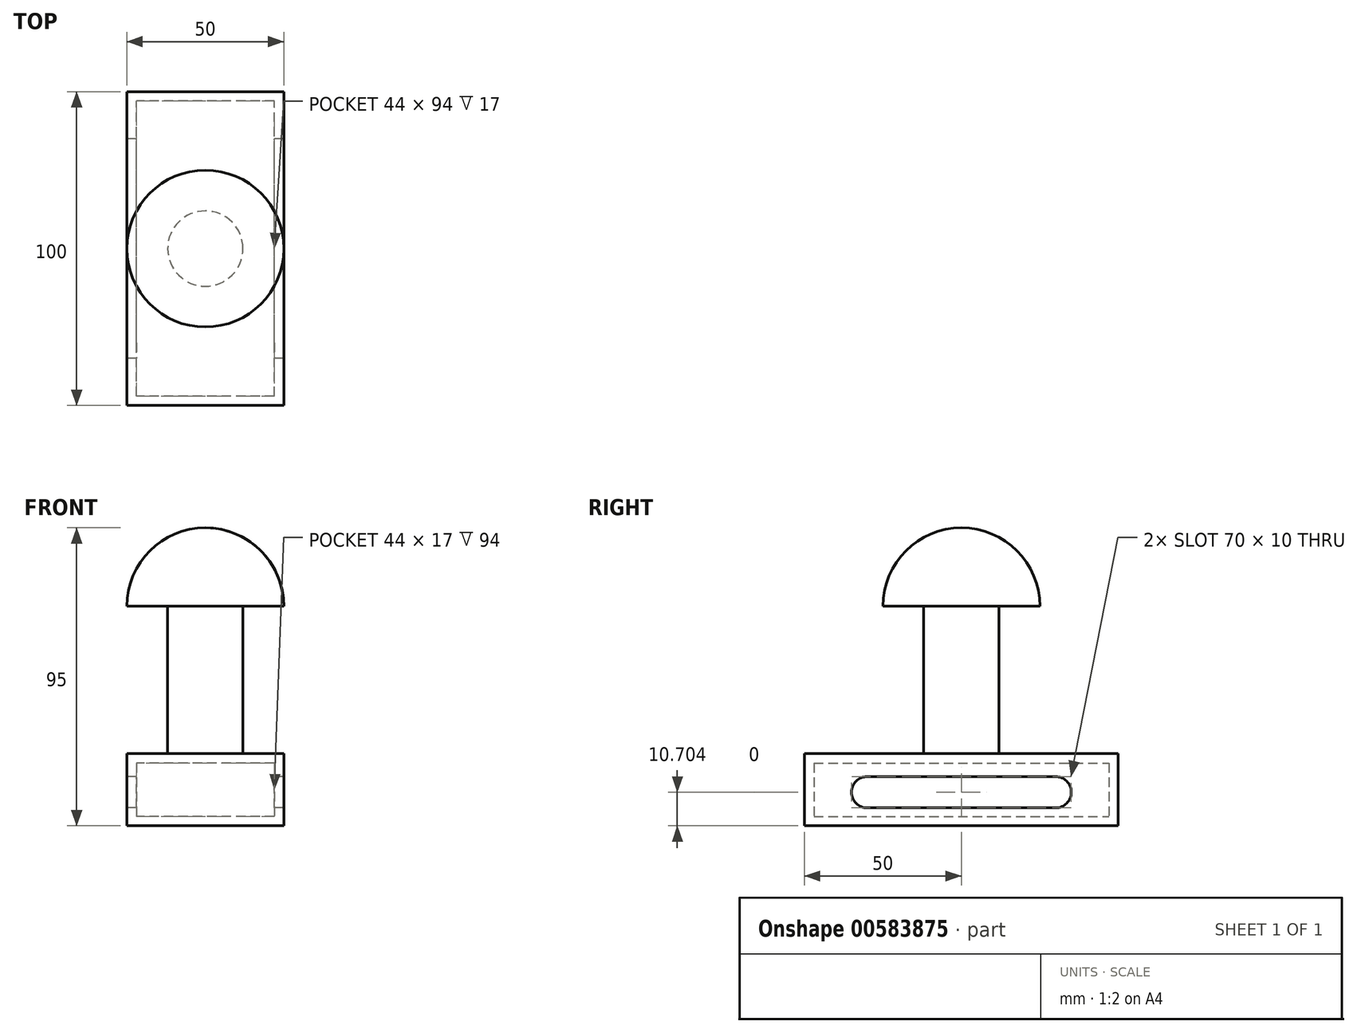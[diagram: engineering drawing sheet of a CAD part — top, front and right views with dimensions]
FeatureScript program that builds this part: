
annotation { "Feature Type Name" : "Feature", "Feature Type Description" : "" }
export const myFeature = defineFeature(function(context is Context, id is Id, definition is map)
    precondition{}
    {
        {
            var Q0;
            Q0=qCreatedBy(makeId("Top.planeOp"),FACE);
            var sketch = newSketch(context, id + "F0", { "sketchPlane" : qUnion([Q0])});
            skLineSegment(sketch, "E0.bottom", {"start": v(25, -50) * mm, "end": v(-25, -50) * mm});
            skLineSegment(sketch, "E0.top", {"start": v(25, 50) * mm, "end": v(-25, 50) * mm});
            skLineSegment(sketch, "E0.left", {"start": v(25, -50) * mm, "end": v(25, 50) * mm});
            skLineSegment(sketch, "E0.right", {"start": v(-25, -50) * mm, "end": v(-25, 50) * mm});
            skPoint(sketch, "E0.middle", {"position": v(0, 0) * mm});
            skLineSegment(sketch, "E1.bottom", {"start": v(22, -47) * mm, "end": v(-22, -47) * mm});
            skLineSegment(sketch, "E1.top", {"start": v(22, 47) * mm, "end": v(-22, 47) * mm});
            skLineSegment(sketch, "E1.left", {"start": v(22, -47) * mm, "end": v(22, 47) * mm});
            skLineSegment(sketch, "E1.right", {"start": v(-22, -47) * mm, "end": v(-22, 47) * mm});
            skSolve(sketch);
        }
        {
            var Q0;
            Q0 = qSketchRegion(id + "F0", true);
            extrude(context, id + "F1", {"entities" : qUnion([Q0]), "depth" : 20 * mm, "offsetDistance" : 25 * mm});
        }
        {
            var Q0;
            Q0=makeQuery(id+"F0.imprint","IMPRINT",FACE,{"disambiguationData":[TD([[makeQuery(id+"F0.imprint","IMPRINT",EDGE,{"derivedFrom":sQuery(id+"F0.wireOp",EDGE,"E1.bottom")}),-1.0]])]});
            var Q1;
            Q1=makeQuery(id+"F0.imprint","IMPRINT",FACE,{"disambiguationData":[TD([[makeQuery(id+"F0.imprint","IMPRINT",EDGE,{"derivedFrom":sQuery(id+"F0.wireOp",EDGE,"E0.bottom")}),-1.0]])]});
            extrude(context, id + "F2", {"entities" : qUnion([Q0, Q1]), "operationType" : NewBodyOperationType.ADD, "depth" : 3 * mm, "offsetDistance" : 25 * mm});
        }
        {
            var Q0;
            Q0=makeQuery(id+"F1.opExtrude","CAP_FACE",FACE,{"disambiguationData":[OSD([sQuery(id+"F0.wireOp",EDGE,"E0.bottom"),sQuery(id+"F0.wireOp",EDGE,"E0.top"),sQuery(id+"F0.wireOp",EDGE,"E0.left"),sQuery(id+"F0.wireOp",EDGE,"E0.right"),sQuery(id+"F0.wireOp",EDGE,"E1.bottom"),sQuery(id+"F0.wireOp",EDGE,"E1.top"),sQuery(id+"F0.wireOp",EDGE,"E1.left"),sQuery(id+"F0.wireOp",EDGE,"E1.right")])],"isStart":false});
            var sketch = newSketch(context, id + "F3", { "sketchPlane" : qUnion([Q0])});
            skLineSegment(sketch, "E2.bottom", {"start": v(-25, 50) * mm, "end": v(25, 50) * mm});
            skLineSegment(sketch, "E2.top", {"start": v(-25, -50) * mm, "end": v(25, -50) * mm});
            skLineSegment(sketch, "E2.left", {"start": v(-25, 50) * mm, "end": v(-25, -50) * mm});
            skLineSegment(sketch, "E2.right", {"start": v(25, 50) * mm, "end": v(25, -50) * mm});
            skCircle(sketch, "E3", {"center": v(0, 0) * mm, "radius": 25 * mm});
            skCircle(sketch, "E4", {"center": v(0, 0) * mm, "radius": 12 * mm});
            skSolve(sketch);
        }
        {
            var Q0;
            Q0=makeQuery(id+"F3.imprint","IMPRINT",FACE,{"disambiguationData":[TD([[makeQuery(id+"F3.imprint","IMPRINT",EDGE,{"derivedFrom":sQuery(id+"F3.wireOp",EDGE,"E2.bottom")}),1.0]])]});
            var Q1;
            Q1=makeQuery(id+"F3.imprint","IMPRINT",FACE,{"disambiguationData":[TD([[makeQuery(id+"F3.imprint","IMPRINT",EDGE,{"derivedFrom":sQuery(id+"F3.wireOp",EDGE,"E3")}),-1.0]])]});
            var Q2;
            Q2=makeQuery(id+"F3.imprint","IMPRINT",FACE,{"disambiguationData":[TD([[makeQuery(id+"F3.imprint","IMPRINT",EDGE,{"derivedFrom":sQuery(id+"F3.wireOp",EDGE,"E3")}),1.0]])]});
            var Q3;
            Q3=makeQuery(id+"F3.imprint","IMPRINT",FACE,{"disambiguationData":[TD([[makeQuery(id+"F3.imprint","IMPRINT",EDGE,{"derivedFrom":sQuery(id+"F3.wireOp",EDGE,"E4")}),1.0]])]});
            var Q4;
            {var subQ0=sQuery(id+"F3.wireOp",EDGE,"E3");var subQ1=makeQuery(id+"F1.opExtrude","CAP_EDGE",EDGE,{"disambiguationData":[OSD([sQuery(id+"F0.wireOp",EDGE,"E1.top")])],"isStart":false});var subQ2=makeQuery(id+"F3.imprint","INTERSECT",VERTEX,{"disambiguationData":[OD(1.0)],"derivedFrom":[subQ1,subQ0]});Q4=makeQuery(id+"F3.imprint","IMPRINT",FACE,{"disambiguationData":[TD([[makeQuery(id+"F3.imprint","IMPRINT",EDGE,{"disambiguationData":[TD([[subQ2,-1.0]])],"derivedFrom":subQ0}),-1.0]])]});}
            var Q5;
            Q5=makeQuery(id+"F3.imprint","IMPRINT",FACE,{"disambiguationData":[TD([[makeQuery(id+"F3.imprint","IMPRINT",EDGE,{"derivedFrom":sQuery(id+"F3.wireOp",EDGE,"E4")}),-1.0]])]});
            var Q6;
            {var subQ0=sQuery(id+"F3.wireOp",EDGE,"E3");var subQ1=makeQuery(id+"F1.opExtrude","CAP_EDGE",EDGE,{"disambiguationData":[OSD([sQuery(id+"F0.wireOp",EDGE,"E1.right")])],"isStart":false});var subQ2=makeQuery(id+"F3.imprint","INTERSECT",VERTEX,{"disambiguationData":[OD(1.0)],"derivedFrom":[subQ1,subQ0]});Q6=makeQuery(id+"F3.imprint","IMPRINT",FACE,{"disambiguationData":[TD([[makeQuery(id+"F3.imprint","IMPRINT",EDGE,{"disambiguationData":[TD([[subQ2,-1.0]])],"derivedFrom":subQ0}),-1.0]])]});}
            var Q7;
            {var subQ0=sQuery(id+"F3.wireOp",EDGE,"E3");var subQ1=makeQuery(id+"F1.opExtrude","CAP_EDGE",EDGE,{"disambiguationData":[OSD([sQuery(id+"F0.wireOp",EDGE,"E1.bottom")])],"isStart":false});var subQ2=makeQuery(id+"F3.imprint","INTERSECT",VERTEX,{"disambiguationData":[OD(1.0)],"derivedFrom":[subQ1,subQ0]});Q7=makeQuery(id+"F3.imprint","IMPRINT",FACE,{"disambiguationData":[TD([[makeQuery(id+"F3.imprint","IMPRINT",EDGE,{"disambiguationData":[TD([[subQ2,-1.0]])],"derivedFrom":subQ0}),-1.0]])]});}
            var Q8;
            {var subQ0=sQuery(id+"F3.wireOp",EDGE,"E3");var subQ1=makeQuery(id+"F1.opExtrude","CAP_EDGE",EDGE,{"disambiguationData":[OSD([sQuery(id+"F0.wireOp",EDGE,"E1.left")])],"isStart":false});var subQ2=makeQuery(id+"F3.imprint","INTERSECT",VERTEX,{"disambiguationData":[OD(0.0)],"derivedFrom":[subQ1,subQ0]});Q8=makeQuery(id+"F3.imprint","IMPRINT",FACE,{"disambiguationData":[TD([[makeQuery(id+"F3.imprint","IMPRINT",EDGE,{"disambiguationData":[TD([[subQ2,-1.0]])],"derivedFrom":subQ0}),-1.0]])]});}
            extrude(context, id + "F4", {"entities" : qUnion([Q0, Q1, Q2, Q3, Q4, Q5, Q6, Q7, Q8]), "operationType" : NewBodyOperationType.ADD, "depth" : 3 * mm, "offsetDistance" : 25 * mm});
        }
        {
            var Q0;
            Q0=makeQuery(id+"F3.imprint","IMPRINT",FACE,{"disambiguationData":[TD([[makeQuery(id+"F3.imprint","IMPRINT",EDGE,{"derivedFrom":sQuery(id+"F3.wireOp",EDGE,"E4")}),1.0]])]});
            extrude(context, id + "F5", {"entities" : qUnion([Q0]), "operationType" : NewBodyOperationType.ADD, "depth" : 50 * mm, "offsetDistance" : 25 * mm});
        }
        {
            var Q0;
            Q0=makeQuery(id+"F5.opExtrude","CAP_FACE",FACE,{"disambiguationData":[OSD([sQuery(id+"F3.wireOp",EDGE,"E4")])],"isStart":false});
            var sketch = newSketch(context, id + "F6", { "sketchPlane" : qUnion([Q0])});
            skCircle(sketch, "E5", {"center": v(0, 0) * mm, "radius": 25 * mm});
            skSolve(sketch);
        }
        {
            var Q0;
            Q0=makeQuery(id+"F6.imprint","IMPRINT",FACE,{"disambiguationData":[TD([[makeQuery(id+"F6.imprint","IMPRINT",EDGE,{"derivedFrom":sQuery(id+"F6.wireOp",EDGE,"E5")}),1.0]])]});
            var Q1;
            Q1=makeQuery(id+"F6.imprint","IMPRINT",FACE,{"disambiguationData":[TD([[makeQuery(id+"F6.imprint","IMPRINT",EDGE,{"derivedFrom":makeQuery(id+"F5.opExtrude","CAP_EDGE",EDGE,{"disambiguationData":[OSD([sQuery(id+"F3.wireOp",EDGE,"E4")])],"isStart":false})}),1.0]])]});
            extrude(context, id + "F7", {"entities" : qUnion([Q0, Q1]), "depth" : 25 * mm, "offsetDistance" : 25 * mm});
        }
        {
            var Q0;
            Q0=makeQuery(id+"F7.opExtrude","CAP_FACE",FACE,{"disambiguationData":[OSD([sQuery(id+"F6.wireOp",EDGE,"E5")])],"isStart":false});
            fillet(context, id + "F8", {"entities" : qUnion([Q0]), "radius" : 25 * mm, "tangentPropagation" : true, "allowEdgeOverflow" : false});
        }
        {
            var Q0;
            Q0=qCreatedBy(makeId("Right.planeOp"),FACE);
            var sketch = newSketch(context, id + "F9", { "sketchPlane" : qUnion([Q0])});
            skLineSegment(sketch, "E6.bottom", {"start": v(-148.29, 8.5) * mm, "end": v(-52.02, 8.5) * mm});
            skLineSegment(sketch, "E6.top", {"start": v(-148.29, -56.79) * mm, "end": v(-52.02, -56.79) * mm});
            skLineSegment(sketch, "E6.left", {"start": v(-148.29, 8.5) * mm, "end": v(-148.29, -56.79) * mm});
            skLineSegment(sketch, "E6.right", {"start": v(-52.02, 8.5) * mm, "end": v(-52.02, -56.79) * mm});
            skCircle(sketch, "E7", {"center": v(-133.41, 41.96) * mm, "radius": 29.59 * mm});
            skArc(sketch, "E8", {"start": v(-148.29, 8.5) * mm, "mid": v(-180.93, -24.15) * mm, "end": v(-148.29, -56.79) * mm});
            skArc(sketch, "E9", {"start": v(-52.02, -56.79) * mm, "mid": v(-19.38, -24.15) * mm, "end": v(-52.02, 8.5) * mm});
            skCircle(sketch, "E10", {"center": v(30, 10.7) * mm, "radius": 5 * mm});
            skCircle(sketch, "E11", {"center": v(-30, 10.7) * mm, "radius": 5 * mm});
            skLineSegment(sketch, "E12", {"start": v(-30, 15.7) * mm, "end": v(30, 15.7) * mm});
            skLineSegment(sketch, "E13", {"start": v(-30, 5.7) * mm, "end": v(30, 5.7) * mm});
            skSolve(sketch);
        }
        {
            var Q0;
            {var subQ0=sQuery(id+"F9.wireOp",EDGE,"E11");var subQ1=makeQuery(id+"F9.imprint","INTERSECT",VERTEX,{"derivedFrom":[subQ0,sQuery(id+"F9.wireOp",EDGE,"E12")]});Q0=makeQuery(id+"F9.imprint","IMPRINT",FACE,{"disambiguationData":[TD([[makeQuery(id+"F9.imprint","IMPRINT",EDGE,{"disambiguationData":[TD([[subQ1,-1.0]])],"derivedFrom":subQ0}),1.0]])]});}
            var Q1;
            {var subQ0=sQuery(id+"F9.wireOp",EDGE,"E12");Q1=makeQuery(id+"F9.imprint","IMPRINT",FACE,{"disambiguationData":[TD([[makeQuery(id+"F9.imprint","IMPRINT",EDGE,{"derivedFrom":subQ0}),-1.0]])]});}
            var Q2;
            {var subQ0=sQuery(id+"F9.wireOp",EDGE,"E10");var subQ1=makeQuery(id+"F9.imprint","INTERSECT",VERTEX,{"derivedFrom":[subQ0,sQuery(id+"F9.wireOp",EDGE,"E12")]});Q2=makeQuery(id+"F9.imprint","IMPRINT",FACE,{"disambiguationData":[TD([[makeQuery(id+"F9.imprint","IMPRINT",EDGE,{"disambiguationData":[TD([[subQ1,-1.0]])],"derivedFrom":subQ0}),1.0]])]});}
            extrude(context, id + "F10", {"entities" : qUnion([Q0, Q1, Q2]), "operationType" : NewBodyOperationType.REMOVE, "endBound" : BoundingType.SYMMETRIC, "depth" : 60 * mm, "offsetDistance" : 25 * mm});
        }
    });
